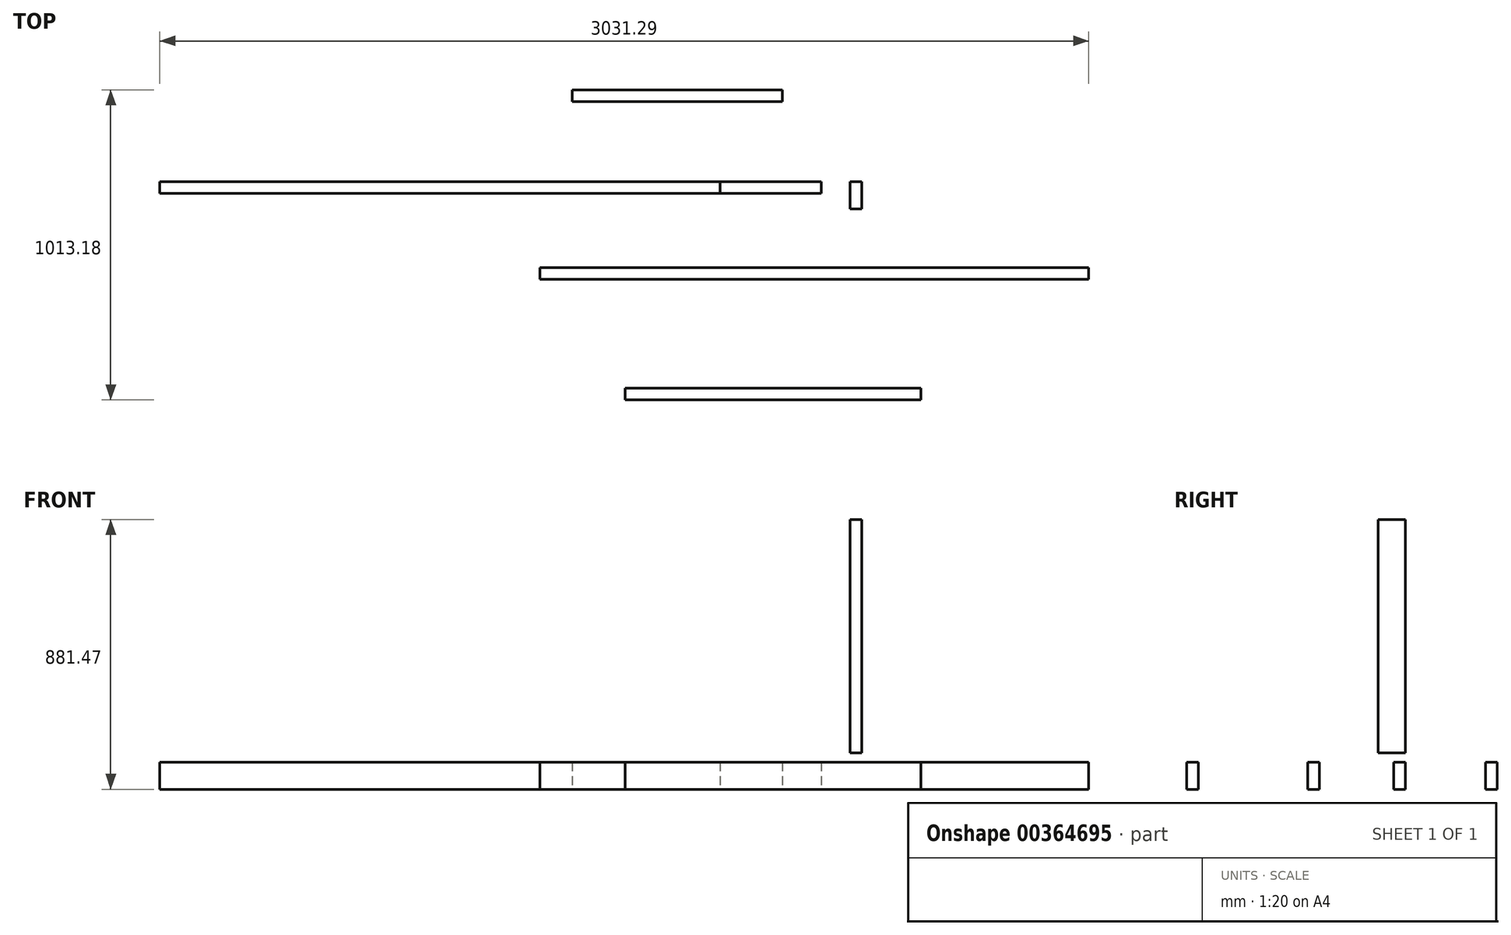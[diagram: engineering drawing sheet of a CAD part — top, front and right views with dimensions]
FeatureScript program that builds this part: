
annotation { "Feature Type Name" : "Feature", "Feature Type Description" : "" }
export const myFeature = defineFeature(function(context is Context, id is Id, definition is map)
    precondition{}
    {
        {
            var Q0;
            Q0=qCreatedBy(makeId("Top.planeOp"),FACE);
            var sketch = newSketch(context, id + "F0", { "sketchPlane" : qUnion([Q0])});
            skLineSegment(sketch, "E0.bottom", {"start": v(0, 0) * mm, "end": v(-1828.8, 0) * mm});
            skLineSegment(sketch, "E0.top", {"start": v(0, -38.1) * mm, "end": v(-1828.8, -38.1) * mm});
            skLineSegment(sketch, "E0.left", {"start": v(0, 0) * mm, "end": v(0, -38.1) * mm});
            skLineSegment(sketch, "E0.right", {"start": v(-1828.8, 0) * mm, "end": v(-1828.8, -38.1) * mm});
            skSolve(sketch);
        }
        {
            var Q0;
            Q0 = qSketchRegion(id + "F0", true);
            extrude(context, id + "F1", {"entities" : qUnion([Q0]), "depth" : 88.9 * mm});
        }
        {
            var Q0;
            Q0=qCreatedBy(makeId("Top.planeOp"),FACE);
            var sketch = newSketch(context, id + "F2", { "sketchPlane" : qUnion([Q0])});
            skLineSegment(sketch, "E1.bottom", {"start": v(0, 0) * mm, "end": v(330.2, 0) * mm});
            skLineSegment(sketch, "E1.top", {"start": v(0, -38.1) * mm, "end": v(330.2, -38.1) * mm});
            skLineSegment(sketch, "E1.left", {"start": v(0, 0) * mm, "end": v(0, -38.1) * mm});
            skLineSegment(sketch, "E1.right", {"start": v(330.2, 0) * mm, "end": v(330.2, -38.1) * mm});
            skSolve(sketch);
        }
        {
            var Q0;
            Q0=makeQuery(id+"F2.imprint","IMPRINT",FACE,{"disambiguationData":[TD([[makeQuery(id+"F2.imprint","IMPRINT",EDGE,{"derivedFrom":sQuery(id+"F2.wireOp",EDGE,"E1.bottom")}),-1.0]])]});
            extrude(context, id + "F3", {"entities" : qUnion([Q0]), "depth" : 88.9 * mm});
        }
        {
            var Q0;
            Q0=qCreatedBy(makeId("Top.planeOp"),FACE);
            var sketch = newSketch(context, id + "F4", { "sketchPlane" : qUnion([Q0])});
            skLineSegment(sketch, "E2.bottom", {"start": v(1202.49, -280.94) * mm, "end": v(-588.21, -280.94) * mm});
            skLineSegment(sketch, "E2.top", {"start": v(1202.49, -319.04) * mm, "end": v(-588.21, -319.04) * mm});
            skLineSegment(sketch, "E2.left", {"start": v(1202.49, -280.94) * mm, "end": v(1202.49, -319.04) * mm});
            skLineSegment(sketch, "E2.right", {"start": v(-588.21, -280.94) * mm, "end": v(-588.21, -319.04) * mm});
            skSolve(sketch);
        }
        {
            var Q0;
            Q0 = qSketchRegion(id + "F4", true);
            extrude(context, id + "F5", {"entities" : qUnion([Q0]), "depth" : 88.9 * mm});
        }
        {
            var Q0;
            Q0=qCreatedBy(makeId("Top.planeOp"),FACE);
            var sketch = newSketch(context, id + "F6", { "sketchPlane" : qUnion([Q0])});
            skLineSegment(sketch, "E3.bottom", {"start": v(654.4, -675.4) * mm, "end": v(-310.8, -675.4) * mm});
            skLineSegment(sketch, "E3.top", {"start": v(654.4, -713.5) * mm, "end": v(-310.8, -713.5) * mm});
            skLineSegment(sketch, "E3.left", {"start": v(654.4, -675.4) * mm, "end": v(654.4, -713.5) * mm});
            skLineSegment(sketch, "E3.right", {"start": v(-310.8, -675.4) * mm, "end": v(-310.8, -713.5) * mm});
            skSolve(sketch);
        }
        {
            var Q0;
            Q0 = qSketchRegion(id + "F6", true);
            extrude(context, id + "F7", {"entities" : qUnion([Q0]), "depth" : 88.9 * mm});
        }
        {
            var Q0;
            Q0=qCreatedBy(makeId("Top.planeOp"),FACE);
            var sketch = newSketch(context, id + "F8", { "sketchPlane" : qUnion([Q0])});
            skLineSegment(sketch, "E4.bottom", {"start": v(-483.42, 299.68) * mm, "end": v(202.38, 299.68) * mm});
            skLineSegment(sketch, "E4.top", {"start": v(-483.42, 261.58) * mm, "end": v(202.38, 261.58) * mm});
            skLineSegment(sketch, "E4.left", {"start": v(-483.42, 299.68) * mm, "end": v(-483.42, 261.58) * mm});
            skLineSegment(sketch, "E4.right", {"start": v(202.38, 299.68) * mm, "end": v(202.38, 261.58) * mm});
            skSolve(sketch);
        }
        {
            var Q0;
            Q0=makeQuery(id+"F8.imprint","IMPRINT",FACE,{"disambiguationData":[TD([[makeQuery(id+"F8.imprint","IMPRINT",EDGE,{"derivedFrom":sQuery(id+"F8.wireOp",EDGE,"E4.bottom")}),-1.0]])]});
            extrude(context, id + "F9", {"entities" : qUnion([Q0]), "depth" : 88.9 * mm});
        }
        {
            var Q0;
            Q0=qCreatedBy(makeId("Front.planeOp"),FACE);
            var sketch = newSketch(context, id + "F10", { "sketchPlane" : qUnion([Q0])});
            skLineSegment(sketch, "E5.bottom", {"start": v(423.23, 881.47) * mm, "end": v(461.33, 881.47) * mm});
            skLineSegment(sketch, "E5.top", {"start": v(423.23, 119.47) * mm, "end": v(461.33, 119.47) * mm});
            skLineSegment(sketch, "E5.left", {"start": v(423.23, 881.47) * mm, "end": v(423.23, 119.47) * mm});
            skLineSegment(sketch, "E5.right", {"start": v(461.33, 881.47) * mm, "end": v(461.33, 119.47) * mm});
            skSolve(sketch);
        }
        {
            var Q0;
            Q0=makeQuery(id+"F10.imprint","IMPRINT",FACE,{"disambiguationData":[TD([[makeQuery(id+"F10.imprint","IMPRINT",EDGE,{"derivedFrom":sQuery(id+"F10.wireOp",EDGE,"E5.bottom")}),-1.0]])]});
            extrude(context, id + "F11", {"entities" : qUnion([Q0]), "depth" : 88.9 * mm});
        }
    });
